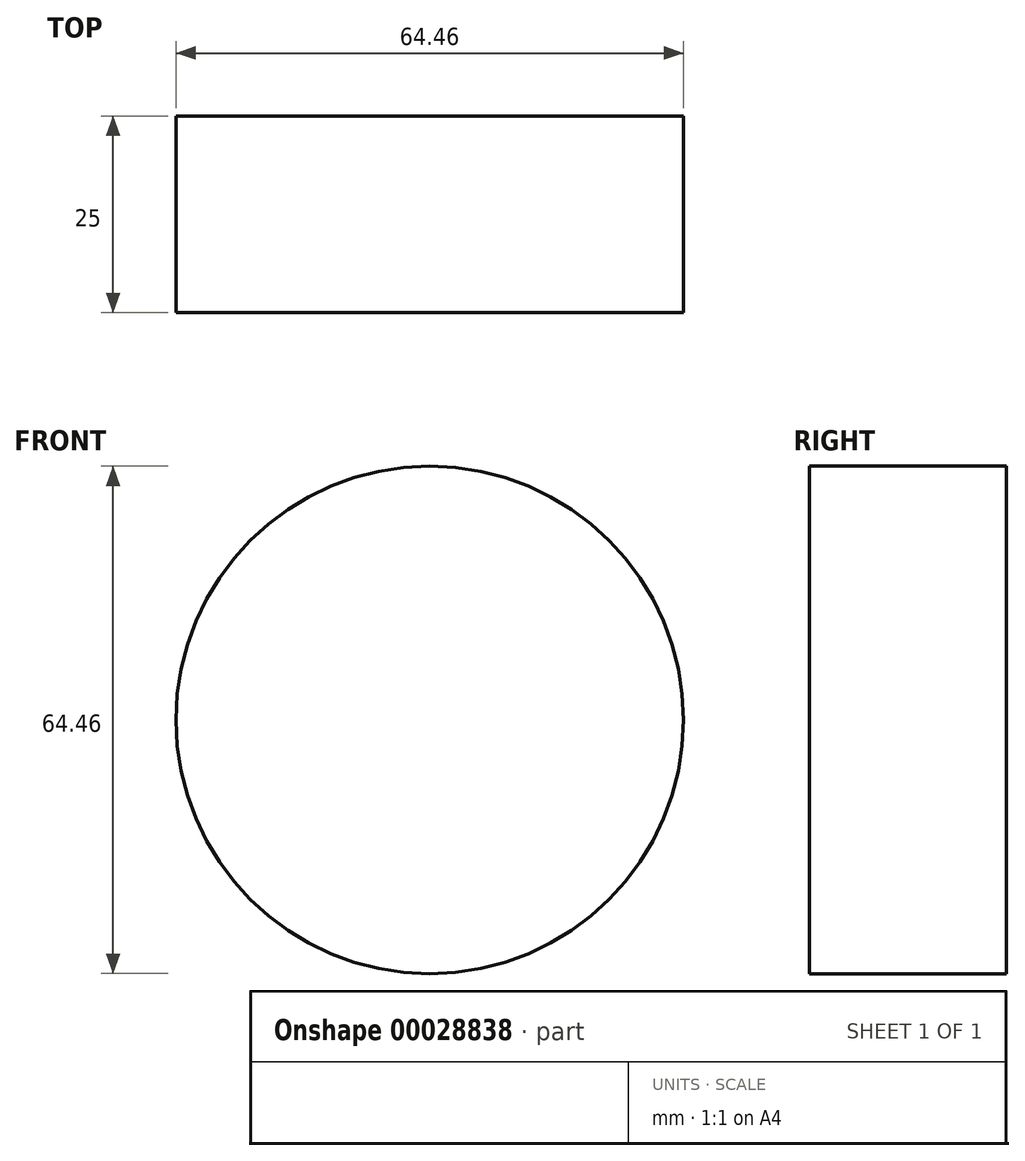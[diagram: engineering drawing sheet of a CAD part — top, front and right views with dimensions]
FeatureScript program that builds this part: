
annotation { "Feature Type Name" : "Feature", "Feature Type Description" : "" }
export const myFeature = defineFeature(function(context is Context, id is Id, definition is map)
    precondition{}
    {
        {
            var Q0;
            Q0=qCreatedBy(makeId("Front.planeOp"),FACE);
            var sketch = newSketch(context, id + "F0", { "sketchPlane" : qUnion([Q0])});
            skCircle(sketch, "E0", {"center": v(0, 0) * mm, "radius": 32.23 * mm});
            skSolve(sketch);
        }
        {
            var Q0;
            Q0=makeQuery(id+"F0.imprint","IMPRINT",FACE,{"disambiguationData":[TD([[makeQuery(id+"F0.imprint","IMPRINT",EDGE,{"derivedFrom":sQuery(id+"F0.wireOp",EDGE,"E0")}),1.0]])]});
            extrude(context, id + "F1", {"entities" : qUnion([Q0]), "oppositeDirection" : true, "depth" : 25 * mm});
        }
    });
